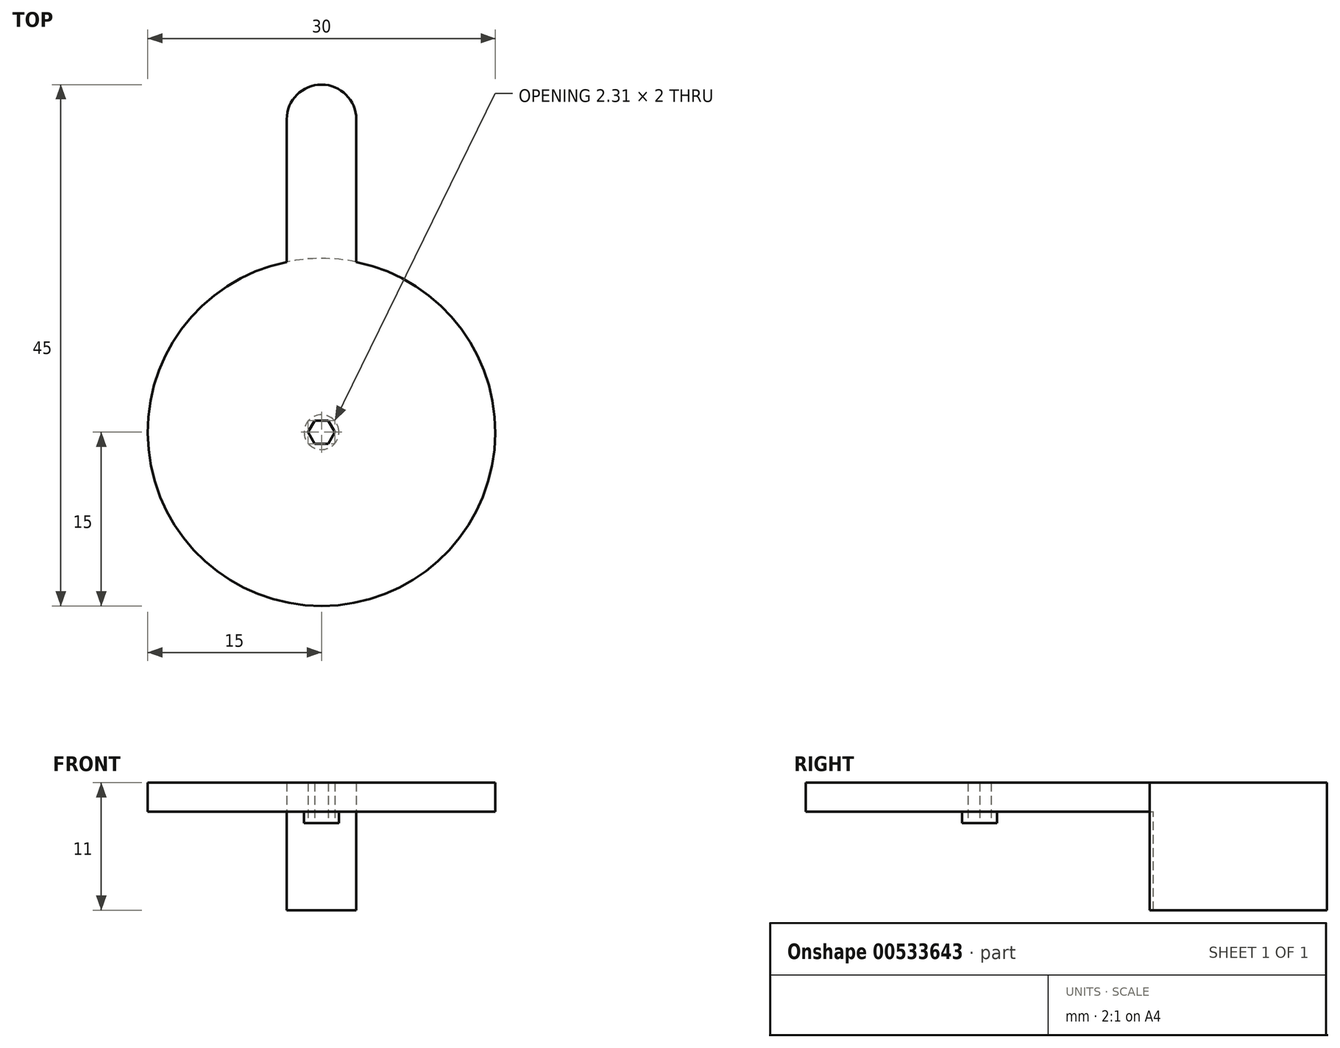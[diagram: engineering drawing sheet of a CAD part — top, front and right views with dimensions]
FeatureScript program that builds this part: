
annotation { "Feature Type Name" : "Feature", "Feature Type Description" : "" }
export const myFeature = defineFeature(function(context is Context, id is Id, definition is map)
    precondition{}
    {
        {
            var Q0;
            Q0=qCreatedBy(makeId("Top.planeOp"),FACE);
            var sketch = newSketch(context, id + "F0", { "sketchPlane" : qUnion([Q0])});
            skCircle(sketch, "E0", {"center": v(0, 0) * mm, "radius": 15 * mm});
            skLineSegment(sketch, "E1.bottom", {"start": v(0, 30) * mm, "end": v(0, 30) * mm});
            skLineSegment(sketch, "E1.top", {"start": v(3, -30) * mm, "end": v(-3, -30) * mm});
            skLineSegment(sketch, "E1.left", {"start": v(3, 27) * mm, "end": v(3, -30) * mm});
            skLineSegment(sketch, "E1.right", {"start": v(-3, 27) * mm, "end": v(-3, -30) * mm});
            skPoint(sketch, "E2.visualSharp", {"position": v(-3, 30) * mm});
            skArc(sketch, "E2.filletArc", {"start": v(0, 30) * mm, "mid": v(-2.12, 29.12) * mm, "end": v(-3, 27) * mm});
            skPoint(sketch, "E3.visualSharp", {"position": v(3, 30) * mm});
            skArc(sketch, "E3.filletArc", {"start": v(3, 27) * mm, "mid": v(2.12, 29.12) * mm, "end": v(0, 30) * mm});
            skCircle(sketch, "E4", {"center": v(0, 0) * mm, "radius": 1 * mm});
            skCircle(sketch, "E5.cCircle", {"center": v(0, 0) * mm, "radius": 1 * mm, "construction": true});
            skLineSegment(sketch, "E5.0", {"start": v(-0.58, 1) * mm, "end": v(0.58, 1) * mm});
            skLineSegment(sketch, "E5.1", {"start": v(0.58, 1) * mm, "end": v(1.15, 0) * mm});
            skLineSegment(sketch, "E5.2", {"start": v(1.15, 0) * mm, "end": v(0.58, -1) * mm});
            skLineSegment(sketch, "E5.3", {"start": v(0.58, -1) * mm, "end": v(-0.58, -1) * mm});
            skLineSegment(sketch, "E5.4", {"start": v(-0.58, -1) * mm, "end": v(-1.15, 0) * mm});
            skLineSegment(sketch, "E5.5", {"start": v(-1.15, 0) * mm, "end": v(-0.58, 1) * mm});
            skPoint(sketch, "E5.0.midPoint", {"position": v(0, 1) * mm});
            skCircle(sketch, "E6", {"center": v(0, 0) * mm, "radius": 1.5 * mm});
            skSolve(sketch);
        }
        {
            var Q0;
            {var subQ0=sQuery(id+"F0.wireOp",EDGE,"E1.right");var subQ1=sQuery(id+"F0.wireOp",EDGE,"E0");var subQ2=makeQuery(id+"F0.imprint","INTERSECT",VERTEX,{"disambiguationData":[OD(0.0)],"derivedFrom":[subQ1,subQ0]});Q0=makeQuery(id+"F0.imprint","IMPRINT",FACE,{"disambiguationData":[TD([[makeQuery(id+"F0.imprint","IMPRINT",EDGE,{"disambiguationData":[TD([[subQ2,-1.0]])],"derivedFrom":subQ1}),1.0]])]});}
            var Q1;
            {var subQ5=sQuery(id+"F0.wireOp",EDGE,"E1.right");var subQ6=sQuery(id+"F0.wireOp",EDGE,"E0");var subQ7=makeQuery(id+"F0.imprint","INTERSECT",VERTEX,{"disambiguationData":[OD(0.0)],"derivedFrom":[subQ6,subQ5]});Q1=makeQuery(id+"F0.imprint","IMPRINT",FACE,{"disambiguationData":[TD([[makeQuery(id+"F0.imprint","IMPRINT",EDGE,{"disambiguationData":[TD([[subQ7,1.0]])],"derivedFrom":subQ6}),1.0]])]});}
            var Q2;
            {var subQ0=sQuery(id+"F0.wireOp",EDGE,"E1.left");var subQ1=sQuery(id+"F0.wireOp",EDGE,"E0");var subQ2=makeQuery(id+"F0.imprint","INTERSECT",VERTEX,{"disambiguationData":[OD(0.0)],"derivedFrom":[subQ1,subQ0]});Q2=makeQuery(id+"F0.imprint","IMPRINT",FACE,{"disambiguationData":[TD([[makeQuery(id+"F0.imprint","IMPRINT",EDGE,{"disambiguationData":[TD([[subQ2,1.0]])],"derivedFrom":subQ1}),1.0]])]});}
            var Q3;
            {var subQ0=sQuery(id+"F0.wireOp",EDGE,"E2.filletArc");Q3=makeQuery(id+"F0.imprint","IMPRINT",FACE,{"disambiguationData":[TD([[makeQuery(id+"F0.imprint","IMPRINT",EDGE,{"derivedFrom":subQ0}),1.0]])]});}
            var Q4;
            Q4=makeQuery(id+"F0.imprint","IMPRINT",FACE,{"disambiguationData":[TD([[makeQuery(id+"F0.imprint","IMPRINT",EDGE,{"derivedFrom":sQuery(id+"F0.wireOp",EDGE,"E6")}),1.0]])]});
            extrude(context, id + "F1", {"entities" : qUnion([Q0, Q1, Q2, Q3, Q4]), "depth" : 2.5 * mm, "offsetDistance" : 25 * mm});
        }
        {
            var Q0;
            {var subQ0=sQuery(id+"F0.wireOp",EDGE,"E2.filletArc");Q0=makeQuery(id+"F0.imprint","IMPRINT",FACE,{"disambiguationData":[TD([[makeQuery(id+"F0.imprint","IMPRINT",EDGE,{"derivedFrom":subQ0}),1.0]])]});}
            extrude(context, id + "F2", {"entities" : qUnion([Q0]), "operationType" : NewBodyOperationType.ADD, "oppositeDirection" : true, "depth" : 8.5 * mm, "offsetDistance" : 25 * mm});
        }
        {
            var Q0;
            Q0=makeQuery(id+"F0.imprint","IMPRINT",FACE,{"disambiguationData":[TD([[makeQuery(id+"F0.imprint","IMPRINT",EDGE,{"derivedFrom":sQuery(id+"F0.wireOp",EDGE,"E6")}),1.0]])]});
            extrude(context, id + "F3", {"entities" : qUnion([Q0]), "operationType" : NewBodyOperationType.ADD, "oppositeDirection" : true, "depth" : 1 * mm, "offsetDistance" : 25 * mm});
        }
    });
